# Revit family: 71984001-51791101
name_source: partatom
category: Air Terminals
units: mm (PartAtom-declared; Revit-internal decimal feet)

## family parameters
Cut with Voids When Loaded = No
Host = Face
Part Type = Normal
Room Calculation Point = No
Round Connector Dimension = Use Diameter
Shared = No

## types (7) — shared parameters
6MonthlyMaintenance = Visually inspect system, clean the fan and ducting if necessary
AirflowRateRange = 0-61
AssetType = Fixed
B = 20 mm  [stored 0.0656168 ft]
CEApproval = Yes
Default Elevation = 1219 mm
DurationUnit = Years
Exclusions = Incorrect Use / Incorrect Installation / Installed by a non-accredited electrician. Customer abuse.
FaceType = LOUVERED
FlowControlType = DAMPER
GF = 10.00°
Grade = Virgin
HasIntegralControl = No
HasSoundAttenuator = No
HasThermalInsulation = No
ISO140001 = Yes
ISO90001 = Yes
IsExtendedWarranty = No
Manufacturer = Airflow Developments Ltd
ManufacturerAddress = Aidelle House
Lancaster Road
Cressex Business Park
High Wycombe
Bucks
HP123QP
ManufacturerTelephone = 01494 525252
ManufacturerWebsite = www.airflow.com
Material = Plastic
MountingType = SURFACE
NBSCode = 90-75-50/370 Air terminals;
NumberOfSlots = 3
PointOfContact = Airflow Developments Ltd
ProductionYear = 2017
ServiceLifeDuration = 10
ServiceLifeType = EXPECTEDSERVICELIFE
Shape = Rectangular
Square_External_Grille_GravityFlap = CADS_AirFlow_White
Uniclass2015 = Pr_65_70_46_01
WarrantyContent = Replacement of part if faulty
WarrantyGuarantor = Airflow Developments Ltd
WarrantyPeriod = 2

## per-type parameters (varying)
| type | A | Color | Constituents | D | Description | Dv | GrossWeight | ModelLabel | ModelReference | NominalHeight | NominalLength | NominalWidth | ReplacementCost | ShippingWeight | Size |
| 140 x 140 x 100mm Dia - White | 140 mm  [stored 0.459318 ft] | White | White | 100 mm  [stored 0.328084 ft] | 140 x 140 x 100mm dia. Gravity Flap (White) | 98 mm  [stored 0.321522 ft] | 0.01 kg | 140 x 140 x 100mm dia. Gravity Flap (White) | 51791101 | 140 mm  [stored 0.459318 ft] | 48 mm  [stored 0.15748 ft] | 140 mm  [stored 0.459318 ft] | 7.944 | 0.01 kg | 48 x 140 x 140 |
| 160 x 160 x 125mm Dia - White | 160 mm  [stored 0.524934 ft] | White | White | 125 mm  [stored 0.410105 ft] | 160 x 160 x 125mm dia. Gravity Flap (White) | 123 mm  [stored 0.403543 ft] | 0.02 kg | 160 x 160 x 125mm dia. Gravity Flap (White) | 9041468 | 160 mm  [stored 0.524934 ft] | 39 mm  [stored 0.127953 ft] | 160 mm  [stored 0.524934 ft] | 11.124 | 0.02 kg | 39 x 160 x 160 |
| 180 x 180 x 150mm Dia - White | 180 mm  [stored 0.590551 ft] | White | White | 150 mm | 180 x 180 x 150mm dia. Gravity Flap (White) | 148 mm  [stored 0.485564 ft] | 0.02 kg | 180 x 180 x 150mm dia. Gravity Flap (White) | 71984001 | 180 mm  [stored 0.590551 ft] | 65 mm  [stored 0.213255 ft] | 180 mm  [stored 0.590551 ft] | 14.268 | 0.02 kg | 65 x 180 x 180 |
| 187 x 187 x 150mm Dia - Brown | 180 mm  [stored 0.590551 ft] | Brown | Brown | 150 mm | 187 x 187 x 150mm dia. Gravity Flap (Brown) | 148 mm  [stored 0.485564 ft] | 0.02 kg | 187 x 187 x 150mm dia. Gravity Flap (Brown) | 90002003 | 180 mm  [stored 0.590551 ft] | 65 mm  [stored 0.213255 ft] | 180 mm  [stored 0.590551 ft] | 14.268 | 0.02 kg | 65 x 180 x 180 |
| 154 x 154 x 100mm Dia - Black | 140 mm  [stored 0.459318 ft] | Black | Black | 100 mm  [stored 0.328084 ft] | 154 x 154 x 100mm dia. Gravity Flap (Black) | 98 mm  [stored 0.321522 ft] | 0.01 kg | 154 x 154 x 100mm dia. Gravity Flap (Black) | 90002004 | 140 mm  [stored 0.459318 ft] | 48 mm  [stored 0.15748 ft] | 140 mm  [stored 0.459318 ft] | 7.944 | 0.01 kg | 48 x 140 x 140 |
| 154 x 154 x 100mm Dia - Brown | 140 mm  [stored 0.459318 ft] | White | White | 100 mm  [stored 0.328084 ft] | 154 x 154 x 100mm dia. Gravity Flap (Brown) | 98 mm  [stored 0.321522 ft] | 0.01 kg | 154 x 154 x 100mm dia. Gravity Flap (Brown) | 90002005 | 140 mm  [stored 0.459318 ft] | 48 mm  [stored 0.15748 ft] | 140 mm  [stored 0.459318 ft] | 7.944 | 0.01 kg | 48 x 140 x 140 |
| 154 x 154 x 100mm Dia - Terracotta | 140 mm  [stored 0.459318 ft] | White | White | 100 mm  [stored 0.328084 ft] | 154 x 154 x 100mm dia. Gravity Flap (Terracotta) | 98 mm  [stored 0.321522 ft] | 0.01 kg | 154 x 154 x 100mm dia. Gravity Flap (Terracotta) | 90002007 | 140 mm  [stored 0.459318 ft] | 48 mm  [stored 0.15748 ft] | 140 mm  [stored 0.459318 ft] | 7.944 | 0.01 kg | 48 x 140 x 140 |

note: [stored X ft] marks values corroborated as IEEE doubles in the binary element streams (Revit-internal decimal feet)

## geometry (parser evidence)
native form markers: Sweep x1
no freeform markers — native parametric forms only
